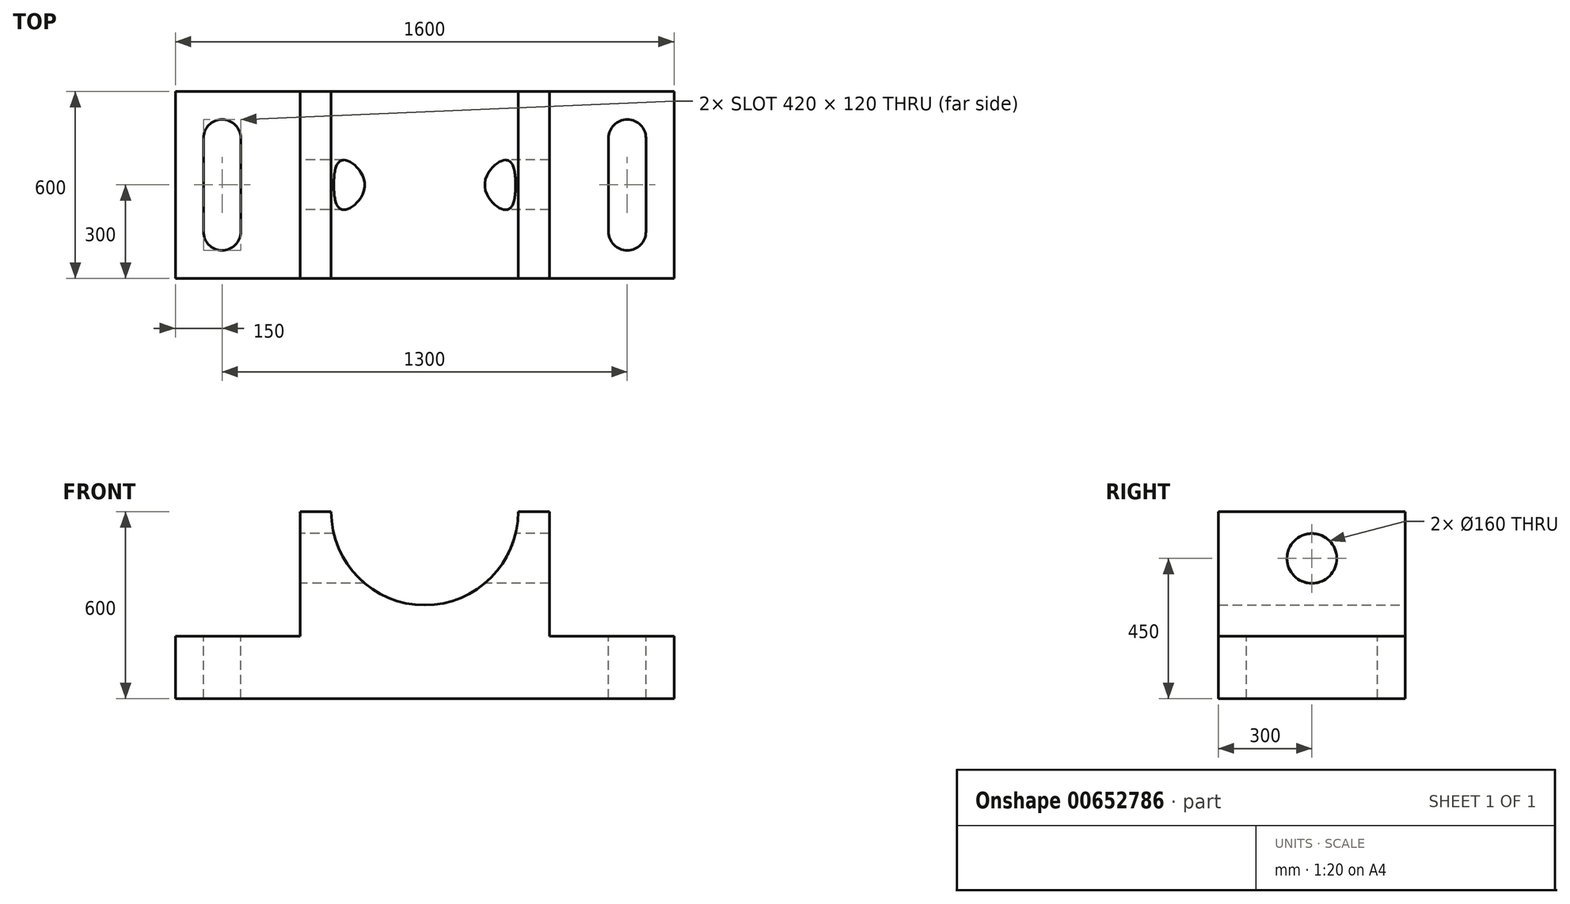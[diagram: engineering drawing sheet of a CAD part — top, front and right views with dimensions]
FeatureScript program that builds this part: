
annotation { "Feature Type Name" : "Feature", "Feature Type Description" : "" }
export const myFeature = defineFeature(function(context is Context, id is Id, definition is map)
    precondition{}
    {
        {
            var Q0;
            Q0=qCreatedBy(makeId("Front.planeOp"),FACE);
            var sketch = newSketch(context, id + "F0", { "sketchPlane" : qUnion([Q0])});
            skLineSegment(sketch, "E0.bottom", {"start": v(-800, 100) * mm, "end": v(-400, 100) * mm});
            skLineSegment(sketch, "E0.top", {"start": v(-800, -100) * mm, "end": v(800, -100) * mm});
            skLineSegment(sketch, "E0.left", {"start": v(-800, 100) * mm, "end": v(-800, -100) * mm});
            skLineSegment(sketch, "E0.right", {"start": v(800, 100) * mm, "end": v(800, -100) * mm});
            skPoint(sketch, "E0.middle", {"position": v(0, 0) * mm});
            skLineSegment(sketch, "E1", {"start": v(-400, 100) * mm, "end": v(-400, 500) * mm});
            skLineSegment(sketch, "E2", {"start": v(400, 100) * mm, "end": v(400, 500) * mm});
            skLineSegment(sketch, "E3", {"start": v(400, 500) * mm, "end": v(300, 500) * mm});
            skLineSegment(sketch, "E4", {"start": v(-400, 500) * mm, "end": v(-300, 500) * mm});
            skLineSegment(sketch, "E5.trimOffspring", {"start": v(400, 100) * mm, "end": v(800, 100) * mm});
            skArc(sketch, "E6", {"start": v(-300, 500) * mm, "mid": v(0, 200) * mm, "end": v(300, 500) * mm});
            skSolve(sketch);
        }
        {
            var Q0;
            Q0 = qSketchRegion(id + "F0", true);
            extrude(context, id + "F1", {"entities" : qUnion([Q0]), "depth" : 600 * mm, "offsetDistance" : 25 * mm});
        }
        {
            var Q0;
            Q0=makeQuery(id+"F1.opExtrude","SWEPT_FACE",FACE,{"disambiguationData":[OSD([sQuery(id+"F0.wireOp",EDGE,"E1")])]});
            var sketch = newSketch(context, id + "F2", { "sketchPlane" : qUnion([Q0])});
            skCircle(sketch, "E7", {"center": v(300, 350) * mm, "radius": 80 * mm});
            skPoint(sketch, "E7.centerSnap0", {"position": v(300, 500) * mm});
            skSolve(sketch);
        }
        {
            var Q0;
            Q0 = qSketchRegion(id + "F2", true);
            extrude(context, id + "F3", {"entities" : qUnion([Q0]), "operationType" : NewBodyOperationType.REMOVE, "endBound" : BoundingType.THROUGH_ALL, "oppositeDirection" : true, "depth" : 25 * mm, "offsetDistance" : 25 * mm});
        }
        {
            var Q0;
            Q0=makeQuery(id+"F1.opExtrude","SWEPT_FACE",FACE,{"disambiguationData":[OSD([sQuery(id+"F0.wireOp",EDGE,"E0.bottom")])]});
            var sketch = newSketch(context, id + "F4", { "sketchPlane" : qUnion([Q0])});
            skLineSegment(sketch, "E8.left", {"start": v(-710, -450) * mm, "end": v(-710, -150) * mm});
            skLineSegment(sketch, "E8.right", {"start": v(-590, -450) * mm, "end": v(-590, -150) * mm});
            skPoint(sketch, "E8.middle", {"position": v(-650, -300) * mm});
            skPoint(sketch, "E8.middle.positionSnap0", {"position": v(-800, -300) * mm});
            skPoint(sketch, "E8.centerSnap0", {"position": v(-800, -300) * mm});
            skArc(sketch, "E9", {"start": v(-590, -150) * mm, "mid": v(-650, -90) * mm, "end": v(-710, -150) * mm});
            skArc(sketch, "E10", {"start": v(-710, -450) * mm, "mid": v(-650, -510) * mm, "end": v(-590, -450) * mm});
            skLineSegment(sketch, "E11.left", {"start": v(590, -450) * mm, "end": v(590, -150) * mm});
            skLineSegment(sketch, "E11.right", {"start": v(710, -450) * mm, "end": v(710, -150) * mm});
            skPoint(sketch, "E11.middle", {"position": v(650, -300) * mm});
            skArc(sketch, "E12", {"start": v(710, -150) * mm, "mid": v(650, -90) * mm, "end": v(590, -150) * mm});
            skArc(sketch, "E13", {"start": v(590, -450) * mm, "mid": v(650, -510) * mm, "end": v(710, -450) * mm});
            skSolve(sketch);
        }
        {
            var Q0;
            Q0 = qSketchRegion(id + "F4", true);
            extrude(context, id + "F5", {"entities" : qUnion([Q0]), "operationType" : NewBodyOperationType.REMOVE, "endBound" : BoundingType.THROUGH_ALL, "oppositeDirection" : true, "depth" : 25 * mm, "offsetDistance" : 25 * mm});
        }
    });
